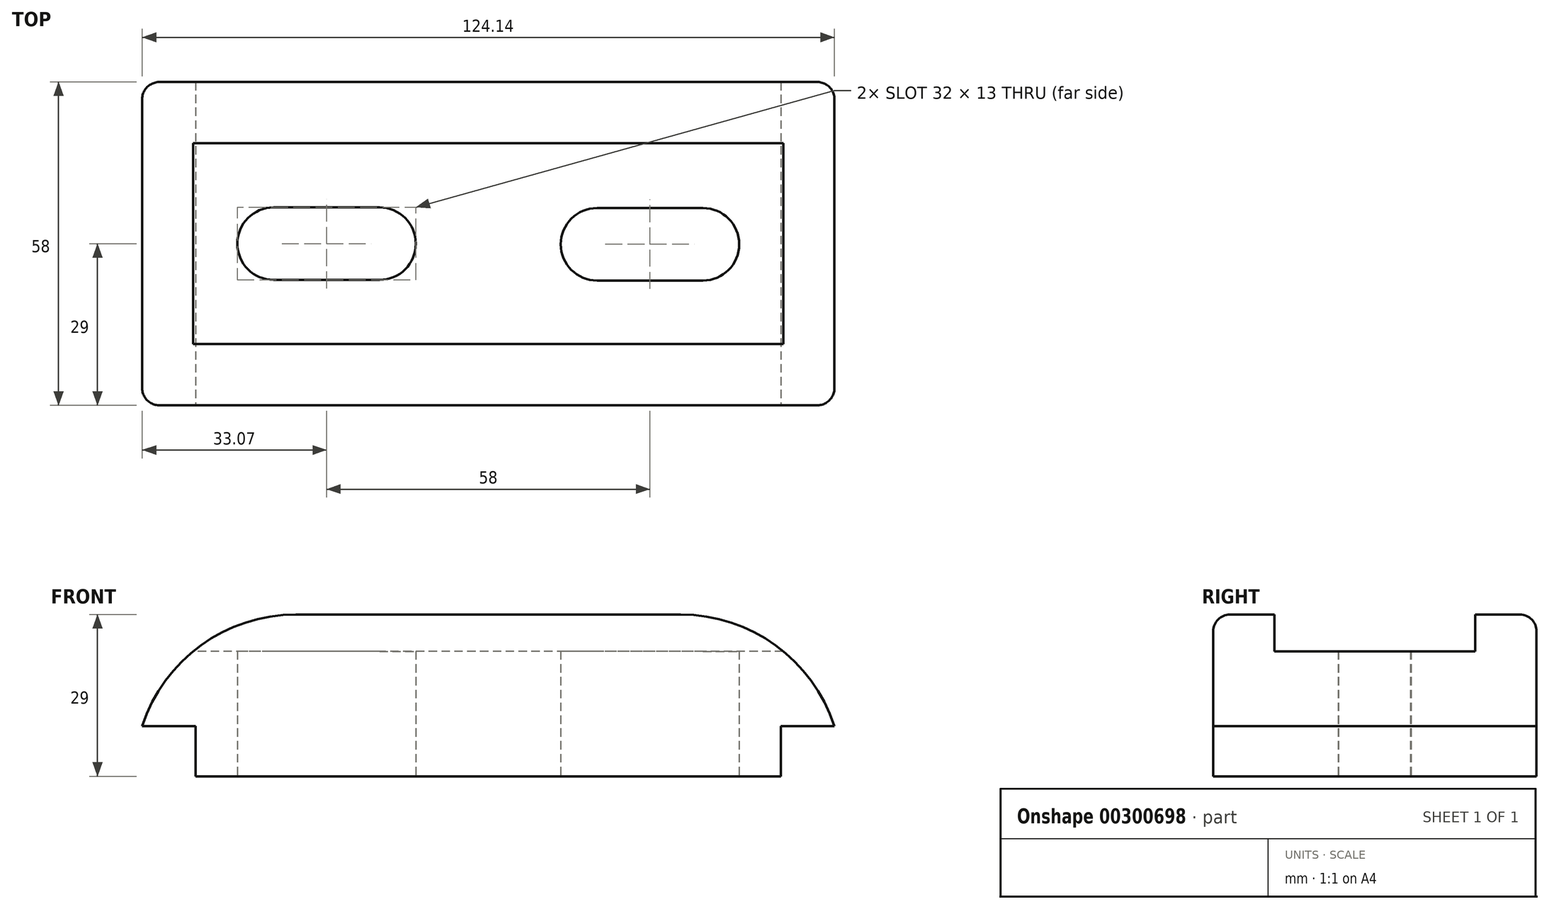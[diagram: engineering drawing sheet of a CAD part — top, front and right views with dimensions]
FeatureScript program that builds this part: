
annotation { "Feature Type Name" : "Feature", "Feature Type Description" : "" }
export const myFeature = defineFeature(function(context is Context, id is Id, definition is map)
    precondition{}
    {
        {
            var Q0;
            Q0=qCreatedBy(makeId("Front.planeOp"),FACE);
            var sketch = newSketch(context, id + "F0", { "sketchPlane" : qUnion([Q0])});
            skArc(sketch, "E0", {"start": v(-62.34, 0) * mm, "mid": v(-53.85, 20.5) * mm, "end": v(-33.34, 29) * mm});
            skArc(sketch, "E1", {"start": v(64.66, 0) * mm, "mid": v(56.17, 20.5) * mm, "end": v(35.66, 29) * mm});
            skLineSegment(sketch, "E2", {"start": v(-62.34, 0) * mm, "end": v(64.66, 0) * mm});
            skLineSegment(sketch, "E3", {"start": v(-33.34, 29) * mm, "end": v(35.66, 29) * mm});
            skLineSegment(sketch, "E4", {"start": v(-60.9, 9) * mm, "end": v(-51.34, 9) * mm});
            skLineSegment(sketch, "E5", {"start": v(-51.34, 9) * mm, "end": v(-51.34, 0) * mm});
            skLineSegment(sketch, "E6", {"start": v(-62.34, 0) * mm, "end": v(-51.34, 0) * mm});
            skLineSegment(sketch, "E7", {"start": v(63.23, 9) * mm, "end": v(53.66, 9) * mm});
            skLineSegment(sketch, "E8", {"start": v(53.66, 9) * mm, "end": v(53.66, 0) * mm});
            skLineSegment(sketch, "E9", {"start": v(53.66, 0) * mm, "end": v(64.66, 0) * mm});
            skSolve(sketch);
        }
        {
            var Q0;
            Q0 = qSketchRegion(id + "F0", true);
            extrude(context, id + "F1", {"entities" : qUnion([Q0]), "depth" : 58 * mm});
        }
        {
            var Q0;
            Q0=makeQuery(id+"F1.opExtrude","CAP_FACE",FACE,{"disambiguationData":[OSD([sQuery(id+"F0.wireOp",EDGE,"E0"),sQuery(id+"F0.wireOp",EDGE,"E1"),sQuery(id+"F0.wireOp",EDGE,"E2"),sQuery(id+"F0.wireOp",EDGE,"E3"),sQuery(id+"F0.wireOp",EDGE,"E6"),sQuery(id+"F0.wireOp",EDGE,"E9")])],"isStart":false});
            var sketch = newSketch(context, id + "F2", { "sketchPlane" : qUnion([Q0])});
            skLineSegment(sketch, "E10", {"start": v(-51.34, 0) * mm, "end": v(-51.34, 9) * mm});
            skLineSegment(sketch, "E11", {"start": v(-51.34, 9) * mm, "end": v(-60.9, 9) * mm});
            skLineSegment(sketch, "E12", {"start": v(63.23, 9) * mm, "end": v(53.66, 9) * mm});
            skLineSegment(sketch, "E13", {"start": v(53.66, 9) * mm, "end": v(53.66, 0) * mm});
            skLineSegment(sketch, "E14", {"start": v(-51.34, 0) * mm, "end": v(-62.34, 0) * mm});
            skLineSegment(sketch, "E15", {"start": v(53.66, 0) * mm, "end": v(64.66, 0) * mm});
            skSolve(sketch);
        }
        {
            var Q0;
            Q0=makeQuery(id+"F2.imprint","IMPRINT",FACE,{"disambiguationData":[TD([[makeQuery(id+"F2.imprint","IMPRINT",EDGE,{"derivedFrom":sQuery(id+"F2.wireOp",EDGE,"E10")}),1.0]])]});
            var Q1;
            {var subQ0=sQuery(id+"F2.wireOp",EDGE,"E12");Q1=makeQuery(id+"F2.imprint","IMPRINT",FACE,{"disambiguationData":[TD([[makeQuery(id+"F2.imprint","IMPRINT",EDGE,{"derivedFrom":subQ0}),1.0]])]});}
            extrude(context, id + "F3", {"entities" : qUnion([Q0, Q1]), "operationType" : NewBodyOperationType.REMOVE, "endBound" : BoundingType.THROUGH_ALL, "oppositeDirection" : true, "depth" : 25 * mm});
        }
        {
            var Q0;
            Q0=qCreatedBy(makeId("Right.planeOp"),FACE);
            var sketch = newSketch(context, id + "F4", { "sketchPlane" : qUnion([Q0])});
            skLineSegment(sketch, "E16", {"start": v(-47, 29) * mm, "end": v(-47, 22.4) * mm});
            skLineSegment(sketch, "E17", {"start": v(-47, 22.4) * mm, "end": v(-11, 22.4) * mm});
            skLineSegment(sketch, "E18", {"start": v(-11, 22.4) * mm, "end": v(-11, 29) * mm});
            skLineSegment(sketch, "E19", {"start": v(-11, 29) * mm, "end": v(-47, 29) * mm});
            skSolve(sketch);
        }
        {
            var Q0;
            Q0 = qSketchRegion(id + "F4", true);
            extrude(context, id + "F5", {"entities" : qUnion([Q0]), "operationType" : NewBodyOperationType.REMOVE, "depth" : 127 * mm, "hasSecondDirection" : true, "secondDirectionOppositeDirection" : true, "secondDirectionDepth" : 127 * mm});
        }
        {
            var Q0;
            Q0=makeQuery(id+"F1.opExtrude","SWEPT_FACE",FACE,{"disambiguationData":[OSD([sQuery(id+"F0.wireOp",EDGE,"E2"),sQuery(id+"F0.wireOp",EDGE,"E6"),sQuery(id+"F0.wireOp",EDGE,"E9")])]});
            var sketch = newSketch(context, id + "F6", { "sketchPlane" : qUnion([Q0])});
            skLineSegment(sketch, "E20", {"start": v(-51.34, 0) * mm, "end": v(53.66, 0) * mm});
            skArc(sketch, "E21", {"start": v(-37.34, 22.5) * mm, "mid": v(-43.84, 29) * mm, "end": v(-37.34, 35.5) * mm});
            skPoint(sketch, "E21.centerSnap0", {"position": v(-51.34, 29) * mm});
            skArc(sketch, "E22", {"start": v(-18.34, 22.5) * mm, "mid": v(-11.84, 29) * mm, "end": v(-18.34, 35.5) * mm});
            skLineSegment(sketch, "E23", {"start": v(-37.34, 22.5) * mm, "end": v(-18.34, 22.5) * mm});
            skLineSegment(sketch, "E24", {"start": v(-37.34, 35.5) * mm, "end": v(-18.34, 35.5) * mm});
            skArc(sketch, "E25", {"start": v(20.66, 22.61) * mm, "mid": v(14.16, 29.11) * mm, "end": v(20.66, 35.61) * mm});
            skArc(sketch, "E26", {"start": v(39.66, 22.61) * mm, "mid": v(46.16, 29.11) * mm, "end": v(39.66, 35.61) * mm});
            skLineSegment(sketch, "E27", {"start": v(20.66, 22.61) * mm, "end": v(39.66, 22.61) * mm});
            skLineSegment(sketch, "E28", {"start": v(20.66, 35.61) * mm, "end": v(39.66, 35.61) * mm});
            skSolve(sketch);
        }
        {
            var Q0;
            Q0 = qSketchRegion(id + "F6", true);
            extrude(context, id + "F7", {"entities" : qUnion([Q0]), "operationType" : NewBodyOperationType.REMOVE, "endBound" : BoundingType.THROUGH_ALL, "oppositeDirection" : true, "depth" : 25 * mm});
        }
        {
            var Q0;
            Q0=makeQuery(id+"F1.opExtrude","CAP_EDGE",EDGE,{"disambiguationData":[OSD([sQuery(id+"F0.wireOp",EDGE,"E3")])],"isStart":false});
            var Q1;
            Q1=makeQuery(id+"F1.opExtrude","CAP_EDGE",EDGE,{"disambiguationData":[OSD([sQuery(id+"F0.wireOp",EDGE,"E3")])],"isStart":true});
            fillet(context, id + "F8", {"entities" : qUnion([Q0, Q1]), "radius" : 3 * mm, "tangentPropagation" : true, "allowEdgeOverflow" : false});
        }
        {
            var Q0;
            Q0 = qSketchRegion(id + "F6", true);
            extrude(context, id + "F9", {"entities" : qUnion([Q0]), "operationType" : NewBodyOperationType.REMOVE, "depth" : 25 * mm});
        }
    });
